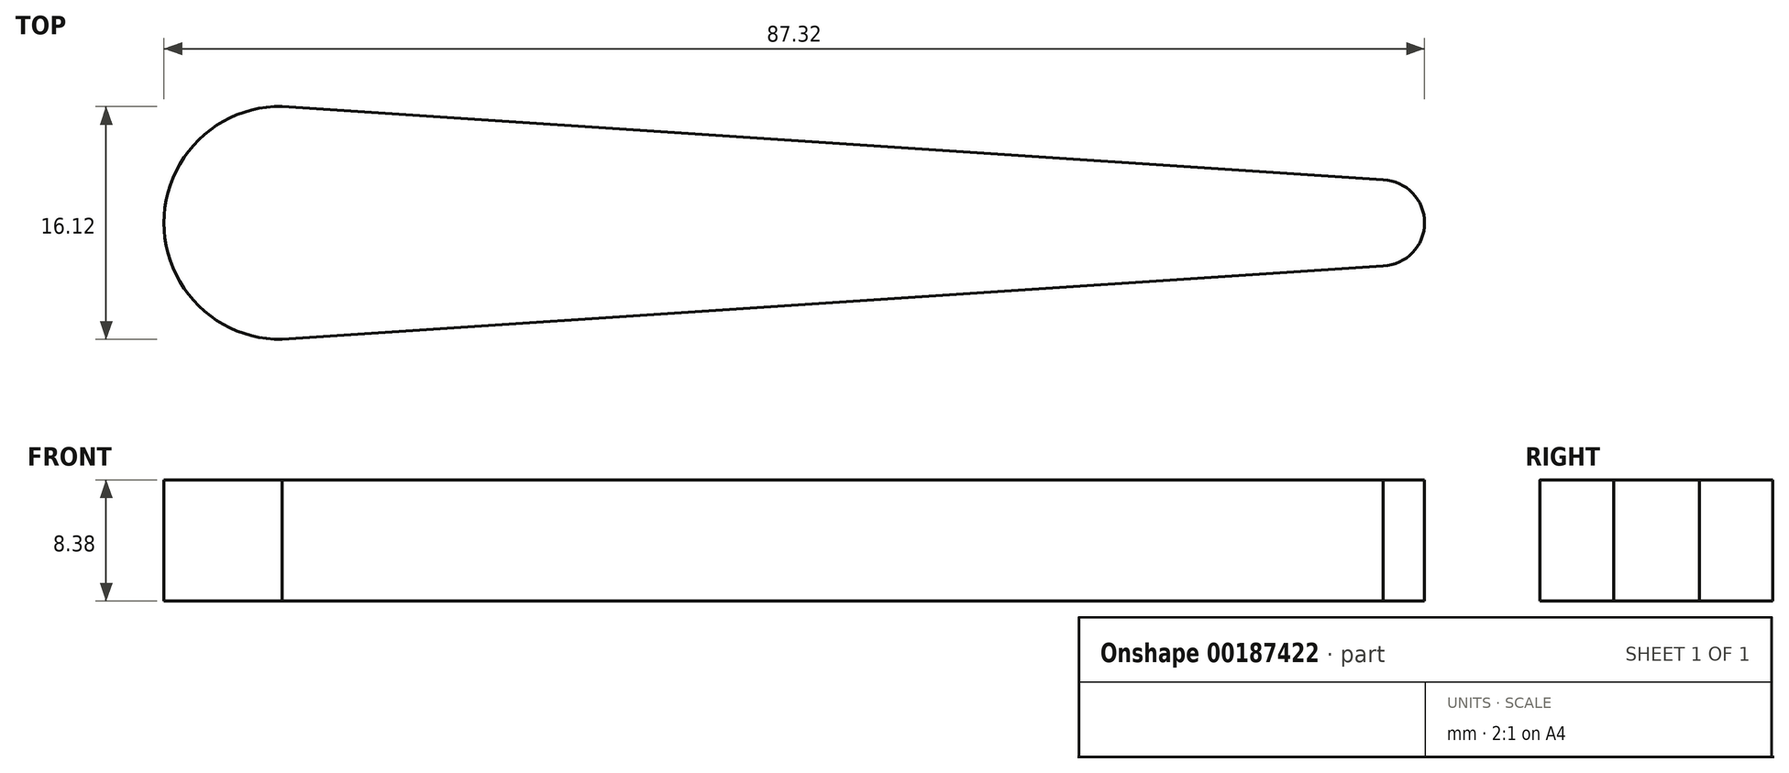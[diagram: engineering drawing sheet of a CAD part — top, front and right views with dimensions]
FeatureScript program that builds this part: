
annotation { "Feature Type Name" : "Feature", "Feature Type Description" : "" }
export const myFeature = defineFeature(function(context is Context, id is Id, definition is map)
    precondition{}
    {
        {
            var Q0;
            Q0=qCreatedBy(makeId("Top.planeOp"),FACE);
            var sketch = newSketch(context, id + "F0", { "sketchPlane" : qUnion([Q0])});
            skArc(sketch, "E0", {"start": v(-56.16, 24.92) * mm, "mid": v(-64.34, 16.86) * mm, "end": v(-56.16, 8.8) * mm});
            skArc(sketch, "E1", {"start": v(20.11, 13.88) * mm, "mid": v(22.98, 16.86) * mm, "end": v(20.11, 19.84) * mm});
            skLineSegment(sketch, "E2", {"start": v(-56.16, 24.92) * mm, "end": v(20.11, 19.84) * mm});
            skLineSegment(sketch, "E3", {"start": v(20.11, 13.88) * mm, "end": v(-56.16, 8.8) * mm});
            skSolve(sketch);
        }
        {
            var Q0;
            Q0 = qSketchRegion(id + "F0", true);
            extrude(context, id + "F1", {"entities" : qUnion([Q0]), "depth" : 8.38 * mm});
        }
    });
